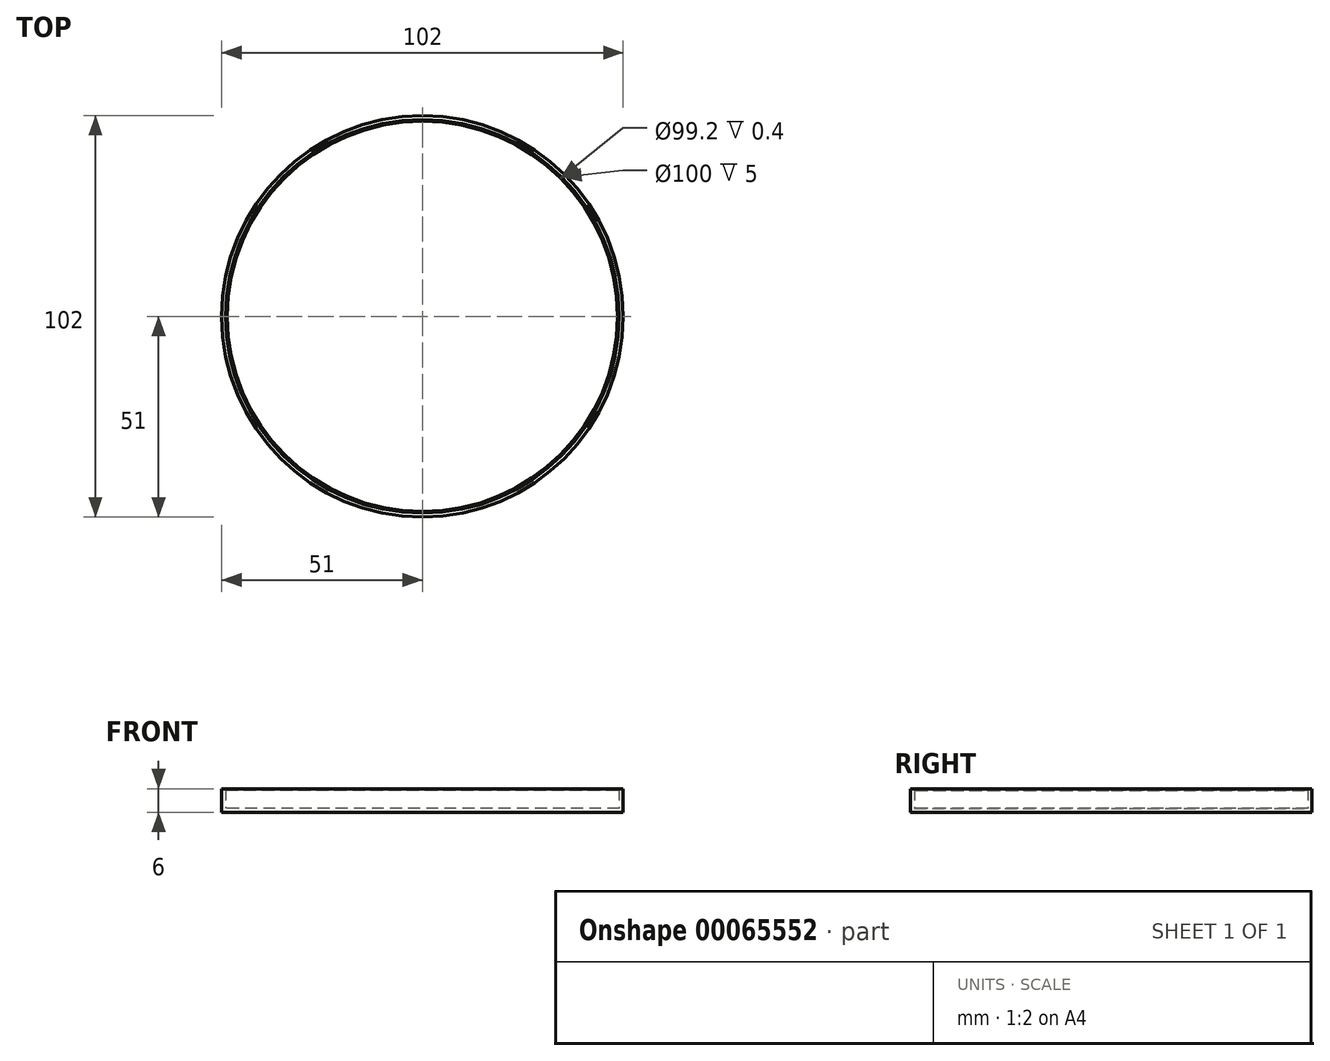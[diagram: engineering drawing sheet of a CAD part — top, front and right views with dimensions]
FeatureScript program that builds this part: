
annotation { "Feature Type Name" : "Feature", "Feature Type Description" : "" }
export const myFeature = defineFeature(function(context is Context, id is Id, definition is map)
    precondition{}
    {
        {
            var Q0;
            Q0=qCreatedBy(makeId("Top.planeOp"),FACE);
            var sketch = newSketch(context, id + "F0", { "sketchPlane" : qUnion([Q0])});
            skCircle(sketch, "E0", {"center": v(0, 0) * mm, "radius": 50 * mm});
            skCircle(sketch, "E1.0", {"center": v(0, 0) * mm, "radius": 51 * mm});
            skCircle(sketch, "E2.0", {"center": v(0, 0) * mm, "radius": 49.6 * mm});
            skSolve(sketch);
        }
        {
            var Q0;
            Q0=makeQuery(id+"F0.imprint","IMPRINT",FACE,{"disambiguationData":[TD([[makeQuery(id+"F0.imprint","IMPRINT",EDGE,{"derivedFrom":sQuery(id+"F0.wireOp",EDGE,"E0")}),1.0]])]});
            var Q1;
            Q1=makeQuery(id+"F0.imprint","IMPRINT",FACE,{"disambiguationData":[TD([[makeQuery(id+"F0.imprint","IMPRINT",EDGE,{"derivedFrom":sQuery(id+"F0.wireOp",EDGE,"E2.0")}),1.0]])]});
            extrude(context, id + "F1", {"entities" : qUnion([Q0, Q1]), "depth" : 1 * mm});
        }
        {
            var Q0;
            Q0=makeQuery(id+"F0.imprint","IMPRINT",FACE,{"disambiguationData":[TD([[makeQuery(id+"F0.imprint","IMPRINT",EDGE,{"derivedFrom":sQuery(id+"F0.wireOp",EDGE,"E0")}),-1.0]])]});
            extrude(context, id + "F2", {"entities" : qUnion([Q0]), "operationType" : NewBodyOperationType.ADD, "depth" : 6 * mm});
        }
        {
            var Q0;
            Q0=makeQuery(id+"F2.opExtrude","CAP_FACE",FACE,{"disambiguationData":[OSD([sQuery(id+"F0.wireOp",EDGE,"E0"),sQuery(id+"F0.wireOp",EDGE,"E1.0")])],"isStart":false});
            var sketch = newSketch(context, id + "F3", { "sketchPlane" : qUnion([Q0])});
            skCircle(sketch, "E3.0", {"center": v(0, 0) * mm, "radius": 49.6 * mm});
            skCircle(sketch, "E4.0", {"center": v(0, 0) * mm, "radius": 55 * mm});
            skLineSegment(sketch, "E5.bottom", {"start": v(-5.57, -64.77) * mm, "end": v(-59.76, -64.77) * mm});
            skLineSegment(sketch, "E5.top", {"start": v(-5.57, 65.78) * mm, "end": v(-59.76, 65.78) * mm});
            skLineSegment(sketch, "E5.left", {"start": v(-5.57, -64.77) * mm, "end": v(-5.57, 65.78) * mm});
            skLineSegment(sketch, "E5.right", {"start": v(-59.76, -64.77) * mm, "end": v(-59.76, 65.78) * mm});
            skLineSegment(sketch, "E6.bottom", {"start": v(4.41, -67) * mm, "end": v(60.48, -67) * mm});
            skLineSegment(sketch, "E6.top", {"start": v(4.41, 76.1) * mm, "end": v(60.48, 76.1) * mm});
            skLineSegment(sketch, "E6.left", {"start": v(4.41, -67) * mm, "end": v(4.41, 76.1) * mm});
            skLineSegment(sketch, "E6.right", {"start": v(60.48, -67) * mm, "end": v(60.48, 76.1) * mm});
            skSolve(sketch);
        }
        {
            var Q0;
            Q0=makeQuery(id+"F3.imprint","IMPRINT",FACE,{"disambiguationData":[TD([[makeQuery(id+"F3.imprint","IMPRINT",EDGE,{"derivedFrom":sQuery(id+"F3.wireOp",EDGE,"E3.0")}),-1.0]])]});
            extrude(context, id + "F4", {"entities" : qUnion([Q0]), "oppositeDirection" : true, "depth" : .4 * mm});
        }
        {
            var Q0;
            Q0 = qSketchRegion(id + "F3", true);
            extrude(context, id + "F5", {"entities" : qUnion([Q0]), "operationType" : NewBodyOperationType.REMOVE, "depth" : 50 * mm});
        }
        {
            var Q0;
            Q0=makeQuery(id+"F4.opExtrude","CAP_EDGE",EDGE,{"disambiguationData":[OSD([sQuery(id+"F0.wireOp",EDGE,"E0")])],"isStart":false});
            chamfer(context, id + "F6", {"entities" : qUnion([Q0]), "width" : .2 * mm});
        }
    });
